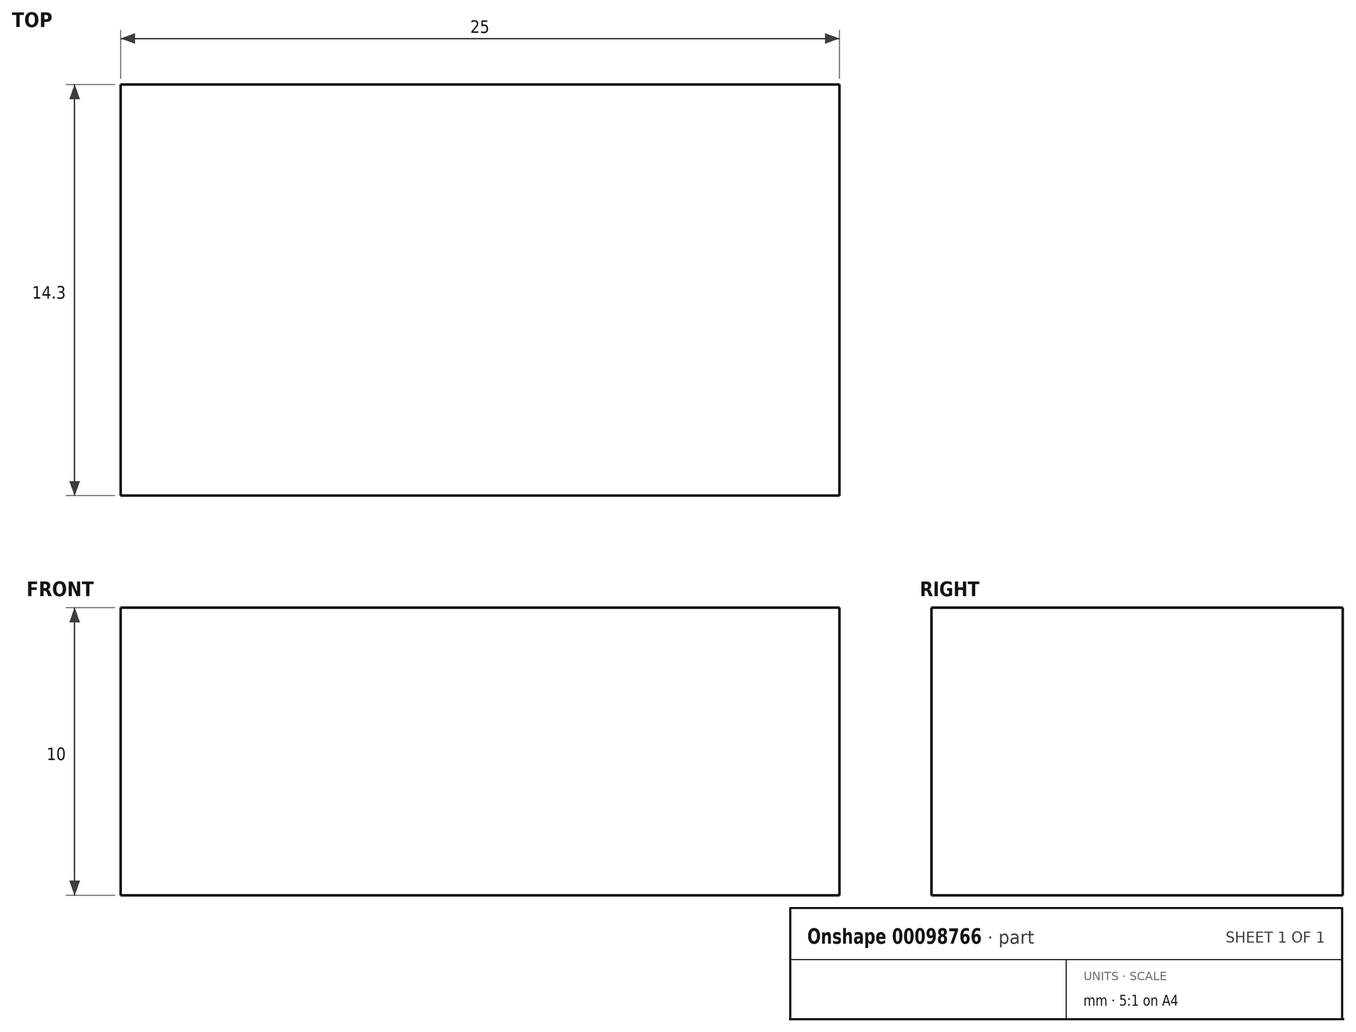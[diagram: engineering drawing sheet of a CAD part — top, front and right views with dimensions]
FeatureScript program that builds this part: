
annotation { "Feature Type Name" : "Feature", "Feature Type Description" : "" }
export const myFeature = defineFeature(function(context is Context, id is Id, definition is map)
    precondition{}
    {
        {
            var Q0;
            Q0=qCreatedBy(makeId("Front.planeOp"),FACE);
            var sketch = newSketch(context, id + "F0", { "sketchPlane" : qUnion([Q0])});
            skLineSegment(sketch, "E0", {"start": v(0, 0) * mm, "end": v(-25, 0) * mm});
            skLineSegment(sketch, "E1", {"start": v(-25, 0) * mm, "end": v(-25, 10) * mm});
            skLineSegment(sketch, "E2", {"start": v(0, 0) * mm, "end": v(0, 10) * mm});
            skLineSegment(sketch, "E3", {"start": v(-25, 10) * mm, "end": v(0, 10) * mm});
            skSolve(sketch);
        }
        {
            var Q0;
            Q0=makeQuery(id+"F0.imprint","IMPRINT",FACE,{"disambiguationData":[TD([[makeQuery(id+"F0.imprint","IMPRINT",EDGE,{"derivedFrom":sQuery(id+"F0.wireOp",EDGE,"E0")}),-1.0]])]});
            extrude(context, id + "F1", {"entities" : qUnion([Q0]), "depth" : 14.3 * mm});
        }
    });
